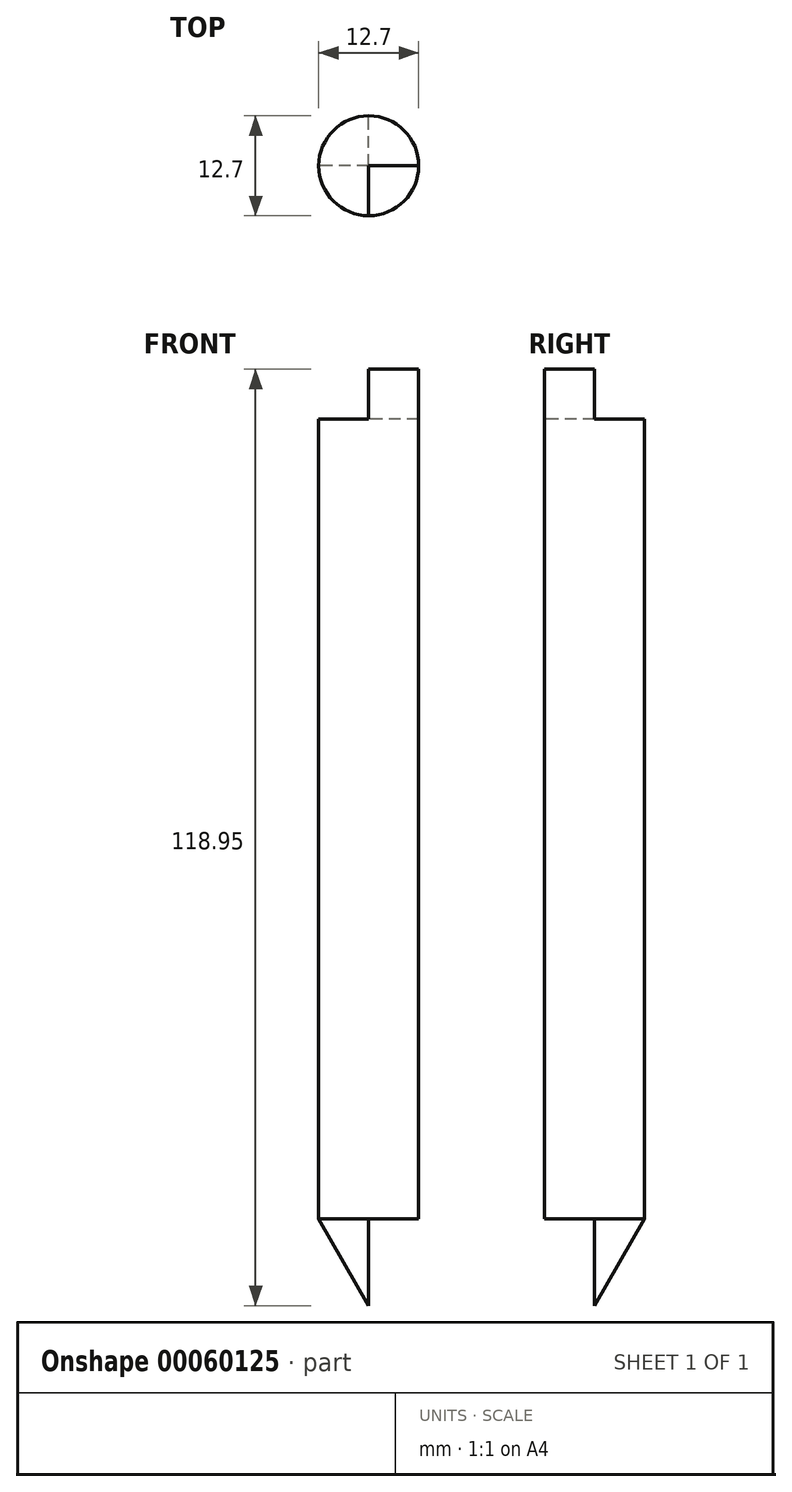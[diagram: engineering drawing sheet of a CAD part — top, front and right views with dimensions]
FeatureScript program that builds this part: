
annotation { "Feature Type Name" : "Feature", "Feature Type Description" : "" }
export const myFeature = defineFeature(function(context is Context, id is Id, definition is map)
    precondition{}
    {
        {
            var Q0;
            Q0=qCreatedBy(makeId("Front.planeOp"),FACE);
            var sketch = newSketch(context, id + "F0", { "sketchPlane" : qUnion([Q0])});
            skLineSegment(sketch, "E0", {"start": v(0, 0) * mm, "end": v(0, -11) * mm});
            skLineSegment(sketch, "E1", {"start": v(0, -11) * mm, "end": v(-6.35, 0) * mm});
            skLineSegment(sketch, "E2", {"start": v(-6.35, 0) * mm, "end": v(0, 0) * mm});
            skSolve(sketch);
        }
        {
            var Q0;
            Q0 = qSketchRegion(id + "F0", true);
            var Q1;
            Q1=sQuery(id+"F0.wireOp",EDGE,"E0");
            revolve(context, id + "F1", {"entities" : qUnion([Q0]), "axis" : qUnion([Q1]), "revolveType" : RevolveType.ONE_DIRECTION, "angle" : 90 * degree});
        }
        {
            var Q0;
            Q0=makeQuery(id+"F1.opRevolve","SWEPT_FACE",FACE,{"disambiguationData":[OSD([sQuery(id+"F0.wireOp",EDGE,"E2")])]});
            var sketch = newSketch(context, id + "F2", { "sketchPlane" : qUnion([Q0])});
            skCircle(sketch, "E3", {"center": v(0, 0) * mm, "radius": 6.35 * mm});
            skSolve(sketch);
        }
        {
            var Q0;
            Q0 = qSketchRegion(id + "F2", true);
            extrude(context, id + "F3", {"entities" : qUnion([Q0]), "operationType" : NewBodyOperationType.ADD, "depth" : 101.6 * mm});
        }
        {
            var Q0;
            Q0=makeQuery(id+"F3.opExtrude","CAP_FACE",FACE,{"disambiguationData":[OSD([sQuery(id+"F2.wireOp",EDGE,"E3")])],"isStart":false});
            var sketch = newSketch(context, id + "F4", { "sketchPlane" : qUnion([Q0])});
            skLineSegment(sketch, "E4", {"start": v(6.35, 0) * mm, "end": v(0, 0) * mm});
            skLineSegment(sketch, "E5", {"start": v(0, 0) * mm, "end": v(0, -6.35) * mm});
            skSolve(sketch);
        }
        {
            var Q0;
            {var subQ0=sQuery(id+"F4.wireOp",EDGE,"E4");Q0=makeQuery(id+"F4.imprint","IMPRINT",FACE,{"disambiguationData":[TD([[makeQuery(id+"F4.imprint","IMPRINT",EDGE,{"derivedFrom":subQ0}),1.0]])]});}
            extrude(context, id + "F5", {"entities" : qUnion([Q0]), "operationType" : NewBodyOperationType.ADD, "depth" : 6.35 * mm});
        }
    });
